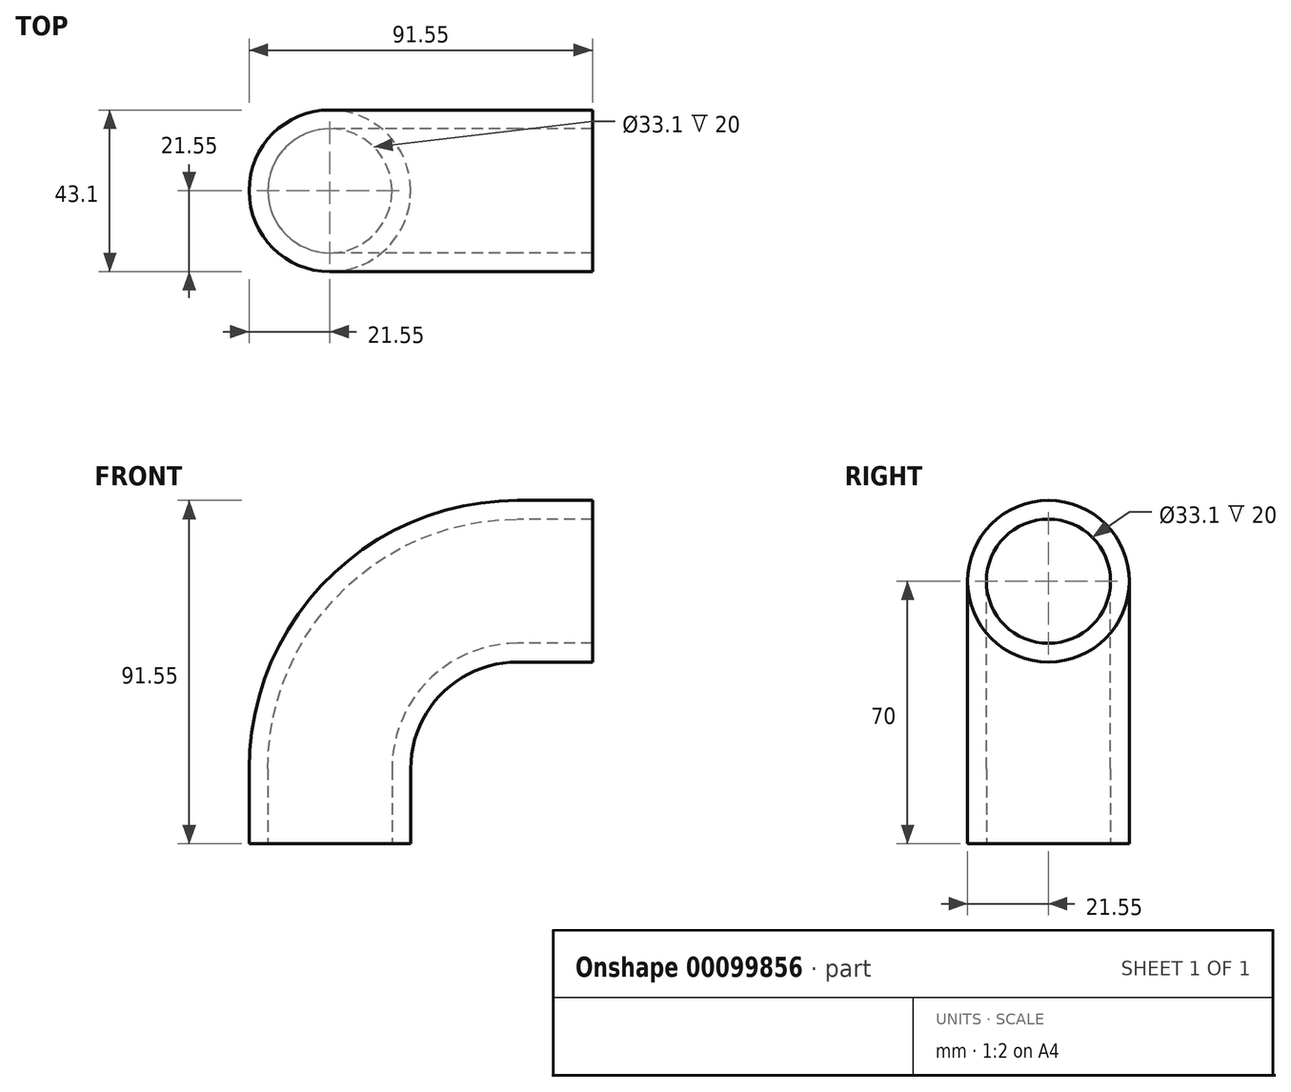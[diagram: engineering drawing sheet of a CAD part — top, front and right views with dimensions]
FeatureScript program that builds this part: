
annotation { "Feature Type Name" : "Feature", "Feature Type Description" : "" }
export const myFeature = defineFeature(function(context is Context, id is Id, definition is map)
    precondition{}
    {
        {
            var Q0;
            Q0=qCreatedBy(makeId("Front.planeOp"),FACE);
            var sketch = newSketch(context, id + "F0", { "sketchPlane" : qUnion([Q0])});
            skLineSegment(sketch, "E0", {"start": v(0, 0) * mm, "end": v(-20, 0) * mm});
            skLineSegment(sketch, "E1", {"start": v(-70, -50) * mm, "end": v(-70, -70) * mm});
            skPoint(sketch, "E2.visualSharp", {"position": v(-70, 0) * mm});
            skArc(sketch, "E2.filletArc", {"start": v(-20, 0) * mm, "mid": v(-55.36, -14.64) * mm, "end": v(-70, -50) * mm});
            skSolve(sketch);
        }
        {
            var Q0;
            Q0=qCreatedBy(makeId("Right.planeOp"),FACE);
            var sketch = newSketch(context, id + "F1", { "sketchPlane" : qUnion([Q0])});
            skCircle(sketch, "E3", {"center": v(0, 0) * mm, "radius": 21.55 * mm});
            skCircle(sketch, "E4", {"center": v(0, 0) * mm, "radius": 16.55 * mm});
            skSolve(sketch);
        }
        {
            var Q0;
            Q0=qSketchRegion(id+"F1",true);
            var Q1;
            Q1=sQuery(id+"F0.wireOp",EDGE,"E0");
            var Q2;
            Q2=sQuery(id+"F0.wireOp",EDGE,"E2.filletArc");
            var Q3;
            Q3=sQuery(id+"F0.wireOp",EDGE,"E1");
            sweep(context, id + "F2", {"profiles" : qUnion([Q0]), "path" : qUnion([Q1, Q2, Q3])});
        }
    });
